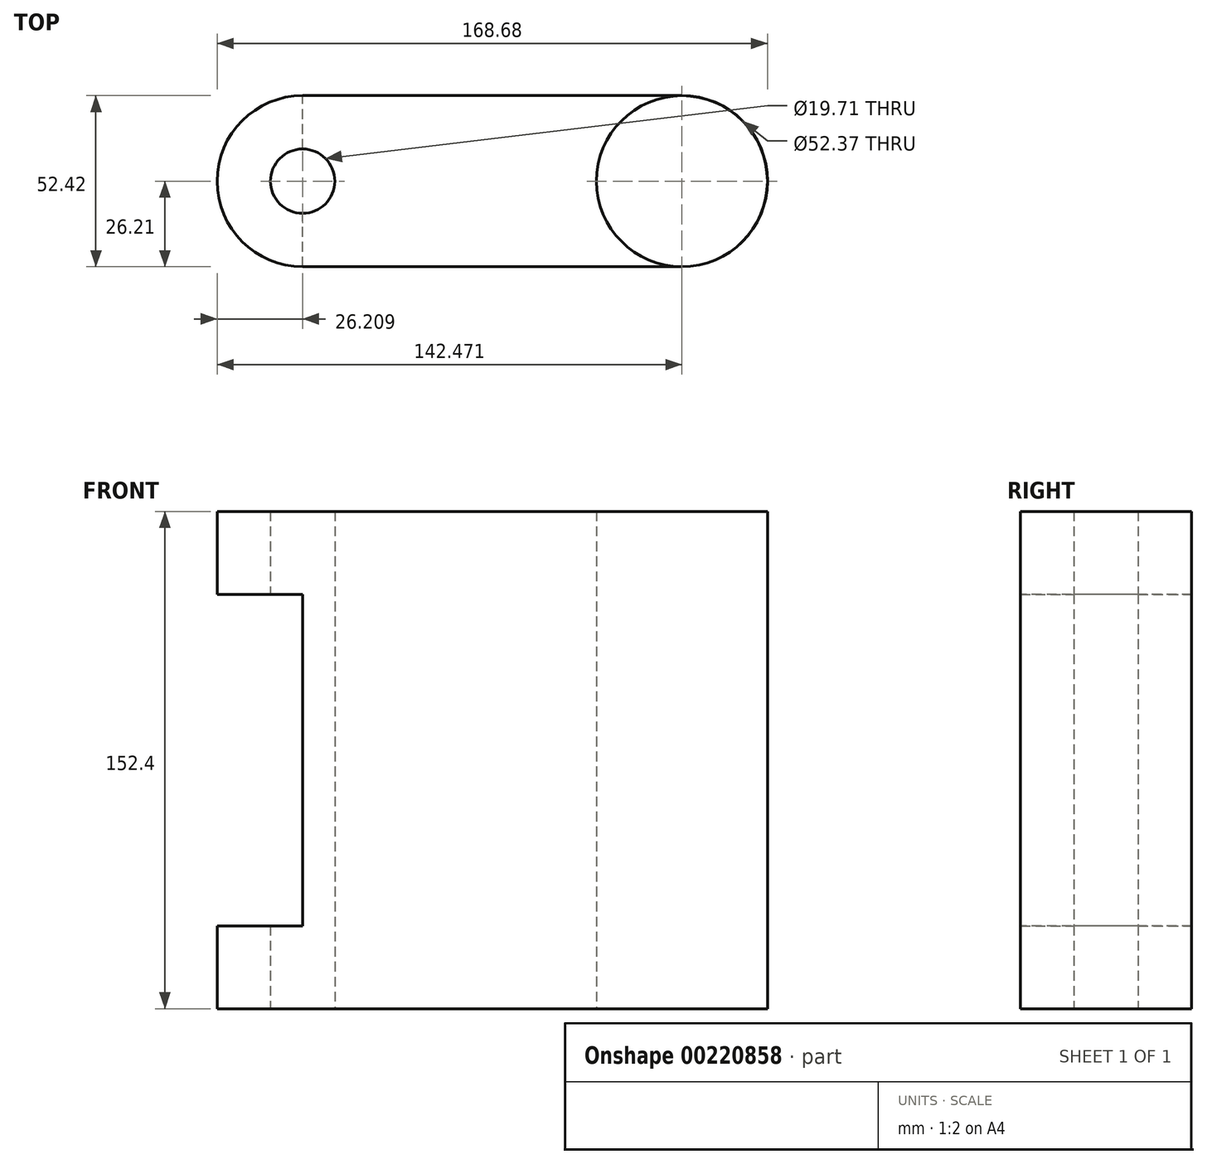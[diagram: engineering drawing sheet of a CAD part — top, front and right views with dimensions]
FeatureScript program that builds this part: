
annotation { "Feature Type Name" : "Feature", "Feature Type Description" : "" }
export const myFeature = defineFeature(function(context is Context, id is Id, definition is map)
    precondition{}
    {
        {
            var Q0;
            Q0=qCreatedBy(makeId("Top.planeOp"),FACE);
            var sketch = newSketch(context, id + "F0", { "sketchPlane" : qUnion([Q0])});
            skLineSegment(sketch, "E0.bottom", {"start": v(58.13, -26.2) * mm, "end": v(-58.13, -26.2) * mm});
            skLineSegment(sketch, "E0.top", {"start": v(58.13, 26.2) * mm, "end": v(-58.13, 26.2) * mm});
            skLineSegment(sketch, "E0.left", {"start": v(58.13, -26.2) * mm, "end": v(58.13, 26.2) * mm});
            skLineSegment(sketch, "E0.right", {"start": v(-58.13, -26.2) * mm, "end": v(-58.13, 26.2) * mm});
            skPoint(sketch, "E0.middle", {"position": v(0, 0) * mm});
            skArc(sketch, "E1", {"start": v(58.13, -26.2) * mm, "mid": v(84.34, 0) * mm, "end": v(58.13, 26.2) * mm});
            skArc(sketch, "E2", {"start": v(-58.13, 26.2) * mm, "mid": v(-84.34, 0) * mm, "end": v(-58.13, -26.2) * mm});
            skCircle(sketch, "E3", {"center": v(58.13, 0) * mm, "radius": 11.1 * mm});
            skCircle(sketch, "E4", {"center": v(-58.13, 0) * mm, "radius": 9.86 * mm});
            skCircle(sketch, "E5", {"center": v(58.13, 0) * mm, "radius": 26.19 * mm});
            skSolve(sketch);
        }
        {
            var Q0;
            {var subQ0=sQuery(id+"F0.wireOp",EDGE,"E5");var subQ1=sQuery(id+"F0.wireOp",EDGE,"E0.left");var subQ2=makeQuery(id+"F0.imprint","INTERSECT",VERTEX,{"disambiguationData":[OD(0.0)],"derivedFrom":[subQ1,subQ0]});Q0=makeQuery(id+"F0.imprint","IMPRINT",FACE,{"disambiguationData":[TD([[makeQuery(id+"F0.imprint","IMPRINT",EDGE,{"disambiguationData":[TD([[subQ2,-1.0]])],"derivedFrom":subQ1}),1.0]])]});}
            var Q1;
            {var subQ0=sQuery(id+"F0.wireOp",EDGE,"E5");var subQ1=sQuery(id+"F0.wireOp",EDGE,"E0.left");var subQ2=makeQuery(id+"F0.imprint","INTERSECT",VERTEX,{"disambiguationData":[OD(0.0)],"derivedFrom":[subQ1,subQ0]});Q1=makeQuery(id+"F0.imprint","IMPRINT",FACE,{"disambiguationData":[TD([[makeQuery(id+"F0.imprint","IMPRINT",EDGE,{"disambiguationData":[TD([[subQ2,-1.0]])],"derivedFrom":subQ1}),-1.0]])]});}
            extrude(context, id + "F1", {"entities" : qUnion([Q0, Q1]), "depth" : 76.2 * mm});
        }
        {
            var Q0;
            Q0 = qSketchRegion(id + "F0", true);
            extrude(context, id + "F2", {"entities" : qUnion([Q0]), "operationType" : NewBodyOperationType.ADD, "depth" : 25.4 * mm});
        }
        {
            var Q0;
            Q0=makeQuery(id+"F1.opExtrude","SWEPT_BODY",BODY,{"disambiguationData":[OSD([sQuery(id+"F0.wireOp",EDGE,"E3"),sQuery(id+"F0.wireOp",EDGE,"E5")])]});
            var Q1;
            Q1=makeQuery(id+"F1.opExtrude","CAP_FACE",FACE,{"disambiguationData":[OSD([sQuery(id+"F0.wireOp",EDGE,"E3"),sQuery(id+"F0.wireOp",EDGE,"E5")])],"isStart":false});
            mirror(context, id + "F3", {"operationType" : NewBodyOperationType.ADD, "entities" : qUnion([Q0]), "mirrorPlane" : qUnion([Q1])});
        }
    });
